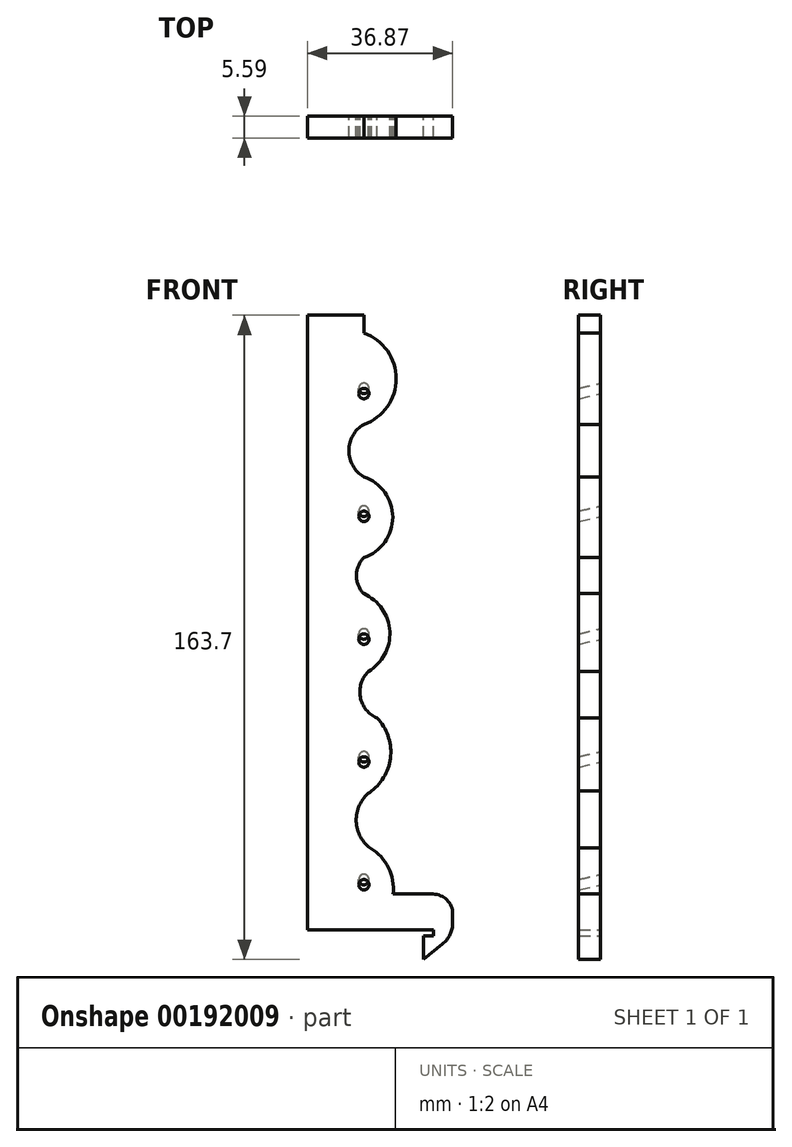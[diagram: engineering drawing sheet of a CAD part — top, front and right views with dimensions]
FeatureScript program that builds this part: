
annotation { "Feature Type Name" : "Feature", "Feature Type Description" : "" }
export const myFeature = defineFeature(function(context is Context, id is Id, definition is map)
    precondition{}
    {
        {
            var Q0;
            Q0=qCreatedBy(makeId("Front.planeOp"),FACE);
            var sketch = newSketch(context, id + "F0", { "sketchPlane" : qUnion([Q0])});
            skLineSegment(sketch, "E0", {"start": v(-18.92, 124.62) * mm, "end": v(-18.92, -31.58) * mm});
            skLineSegment(sketch, "E1", {"start": v(-18.92, 124.62) * mm, "end": v(-4.62, 124.62) * mm});
            skLineSegment(sketch, "E2", {"start": v(10.58, -33.08) * mm, "end": v(13.08, -33.08) * mm});
            skLineSegment(sketch, "E3", {"start": v(-18.92, -31.58) * mm, "end": v(13.08, -31.58) * mm});
            skLineSegment(sketch, "E4", {"start": v(13.08, -33.08) * mm, "end": v(13.08, -31.58) * mm});
            skLineSegment(sketch, "E5", {"start": v(10.58, -33.08) * mm, "end": v(10.58, -39.08) * mm});
            skLineSegment(sketch, "E6", {"start": v(10.58, -39.08) * mm, "end": v(17.95, -33.08) * mm});
            skLineSegment(sketch, "E7", {"start": v(17.95, -33.08) * mm, "end": v(17.95, -22.48) * mm});
            skLineSegment(sketch, "E8", {"start": v(17.95, -22.48) * mm, "end": v(2.81, -22.48) * mm});
            skArc(sketch, "E9", {"start": v(-3.49, 34.05) * mm, "mid": v(-5.5, 27.56) * mm, "end": v(-1.25, 22.25) * mm});
            skArc(sketch, "E10", {"start": v(2.81, -22.48) * mm, "mid": v(1.63, -15.76) * mm, "end": v(-3.02, -10.76) * mm});
            skArc(sketch, "E11", {"start": v(-2.68, 3.72) * mm, "mid": v(2.19, 12.67) * mm, "end": v(-1.25, 22.25) * mm});
            skArc(sketch, "E12", {"start": v(-2.68, 3.72) * mm, "mid": v(-6.55, -3.43) * mm, "end": v(-3.02, -10.76) * mm});
            skLineSegment(sketch, "E13", {"start": v(-4.62, -47.9) * mm, "end": v(-4.62, 124.62) * mm, "construction": true});
            skArc(sketch, "E14", {"start": v(-3.49, 34.05) * mm, "mid": v(1.96, 44.3) * mm, "end": v(-4.62, 53.85) * mm});
            skLineSegment(sketch, "E15", {"start": v(-4.62, 120.08) * mm, "end": v(-4.62, 124.62) * mm});
            skArc(sketch, "E16", {"start": v(-4.62, 63.01) * mm, "mid": v(-6.53, 58.43) * mm, "end": v(-4.62, 53.85) * mm});
            skArc(sketch, "E17", {"start": v(-4.62, 63.01) * mm, "mid": v(2.72, 73.28) * mm, "end": v(-4.62, 83.55) * mm});
            skArc(sketch, "E18", {"start": v(-4.62, 96.87) * mm, "mid": v(-8.44, 90.21) * mm, "end": v(-4.62, 83.55) * mm});
            skArc(sketch, "E19", {"start": v(-4.62, 96.87) * mm, "mid": v(3.6, 108.48) * mm, "end": v(-4.62, 120.08) * mm});
            skSolve(sketch);
        }
        {
            var Q0;
            Q0=qCreatedBy(makeId("Front.planeOp"),FACE);
            var sketch = newSketch(context, id + "F1", { "sketchPlane" : qUnion([Q0])});
            skLineSegment(sketch, "E20", {"start": v(-34.42, -18.78) * mm, "end": v(36.84, -18.78) * mm, "construction": true});
            skSolve(sketch);
        }
        {
            var Q0;
            Q0=qCreatedBy(makeId("Front.planeOp"),FACE);
            var sketch = newSketch(context, id + "F2", { "sketchPlane" : qUnion([Q0])});
            skLineSegment(sketch, "E21", {"start": v(24.36, 12.42) * mm, "end": v(-43.96, 12.42) * mm, "construction": true});
            skSolve(sketch);
        }
        {
            var Q0;
            Q0=qCreatedBy(makeId("Front.planeOp"),FACE);
            var sketch = newSketch(context, id + "F3", { "sketchPlane" : qUnion([Q0])});
            skLineSegment(sketch, "E22", {"start": v(22.2, 43.62) * mm, "end": v(-38.2, 43.62) * mm, "construction": true});
            skLineSegment(sketch, "E23", {"start": v(-44.47, 74.82) * mm, "end": v(24.47, 74.82) * mm, "construction": true});
            skLineSegment(sketch, "E24", {"start": v(-44.4, 106.02) * mm, "end": v(24.55, 106.02) * mm, "construction": true});
            skSolve(sketch);
        }
        {
            var Q0;
            Q0=sQuery(id+"F1.wireOp",EDGE,"E20");
            cPlane(context, id + "F4", {"entities" : qUnion([Q0]), "cplaneType" : CPlaneType.LINE_ANGLE, "offset" : 25 * mm, "angle" : 13.27 * degree, "width" : 150 * mm, "height" : 150 * mm});
        }
        {
            var Q0;
            Q0=sQuery(id+"F2.wireOp",EDGE,"E21");
            cPlane(context, id + "F5", {"entities" : qUnion([Q0]), "cplaneType" : CPlaneType.LINE_ANGLE, "offset" : 25 * mm, "angle" : 346.73 * degree, "width" : 150 * mm, "height" : 150 * mm});
        }
        {
            var Q0;
            Q0=sQuery(id+"F3.wireOp",EDGE,"E22");
            cPlane(context, id + "F6", {"entities" : qUnion([Q0]), "cplaneType" : CPlaneType.LINE_ANGLE, "offset" : 25 * mm, "angle" : 346.73 * degree, "width" : 150 * mm, "height" : 150 * mm});
        }
        {
            var Q0;
            Q0=qCreatedBy(id+"F4.planeOp",FACE);
            var sketch = newSketch(context, id + "F7", { "sketchPlane" : qUnion([Q0])});
            skCircle(sketch, "E25", {"center": v(4.62, -18.28) * mm, "radius": 1.3 * mm});
            skSolve(sketch);
        }
        {
            var Q0;
            Q0=qCreatedBy(id+"F5.planeOp",FACE);
            var sketch = newSketch(context, id + "F8", { "sketchPlane" : qUnion([Q0])});
            skCircle(sketch, "E26", {"center": v(-4.62, 12.09) * mm, "radius": 1.3 * mm});
            skSolve(sketch);
        }
        {
            var Q0;
            Q0=qCreatedBy(id+"F6.planeOp",FACE);
            var sketch = newSketch(context, id + "F9", { "sketchPlane" : qUnion([Q0])});
            skCircle(sketch, "E27", {"center": v(-4.62, 42.46) * mm, "radius": 1.3 * mm});
            skSolve(sketch);
        }
        {
            var Q0;
            Q0=sQuery(id+"F3.wireOp",EDGE,"E23");
            cPlane(context, id + "F10", {"entities" : qUnion([Q0]), "cplaneType" : CPlaneType.LINE_ANGLE, "offset" : 25 * mm, "angle" : 13.27 * degree, "width" : 150 * mm, "height" : 150 * mm});
        }
        {
            var Q0;
            Q0=sQuery(id+"F3.wireOp",EDGE,"E24");
            cPlane(context, id + "F11", {"entities" : qUnion([Q0]), "cplaneType" : CPlaneType.LINE_ANGLE, "offset" : 25 * mm, "angle" : 13.27 * degree, "width" : 150 * mm, "height" : 150 * mm});
        }
        {
            var Q0;
            Q0=qCreatedBy(id+"F10.planeOp",FACE);
            var sketch = newSketch(context, id + "F12", { "sketchPlane" : qUnion([Q0])});
            skCircle(sketch, "E28", {"center": v(4.62, 72.82) * mm, "radius": 1.3 * mm});
            skSolve(sketch);
        }
        {
            var Q0;
            Q0=qCreatedBy(id+"F11.planeOp",FACE);
            var sketch = newSketch(context, id + "F13", { "sketchPlane" : qUnion([Q0])});
            skCircle(sketch, "E29", {"center": v(4.62, 103.19) * mm, "radius": 1.3 * mm});
            skSolve(sketch);
        }
        {
            var Q0;
            Q0=makeQuery(id+"F0.imprint","IMPRINT",FACE,{"disambiguationData":[TD([[makeQuery(id+"F0.imprint","IMPRINT",EDGE,{"derivedFrom":sQuery(id+"F0.wireOp",EDGE,"E0")}),1.0]])]});
            extrude(context, id + "F14", {"entities" : qUnion([Q0]), "depth" : 5.6 * mm});
        }
        {
            var Q0;
            Q0 = qSketchRegion(id + "F7", true);
            var Q1;
            Q1 = qSketchRegion(id + "F8", true);
            var Q2;
            Q2 = qSketchRegion(id + "F9", true);
            var Q3;
            Q3 = qSketchRegion(id + "F13", true);
            var Q4;
            Q4 = qSketchRegion(id + "F12", true);
            extrude(context, id + "F15", {"entities" : qUnion([Q0, Q1, Q2, Q3, Q4]), "operationType" : NewBodyOperationType.REMOVE, "endBound" : BoundingType.SYMMETRIC, "oppositeDirection" : true, "depth" : 25 * mm});
        }
        {
            var Q0;
            Q0=makeQuery(id+"F14.opExtrude","SWEPT_EDGE",EDGE,{"disambiguationData":[OSD([sQuery(id+"F0.wireOp",EDGE,"E7"),sQuery(id+"F0.wireOp",EDGE,"E8")])]});
            fillet(context, id + "F16", {"entities" : qUnion([Q0]), "radius" : 5 * mm, "tangentPropagation" : true, "allowEdgeOverflow" : false});
        }
        {
            var Q0;
            Q0=makeQuery(id+"F14.opExtrude","SWEPT_EDGE",EDGE,{"disambiguationData":[OSD([sQuery(id+"F0.wireOp",EDGE,"E6"),sQuery(id+"F0.wireOp",EDGE,"E7")])]});
            fillet(context, id + "F17", {"entities" : qUnion([Q0]), "radius" : 7 * mm, "tangentPropagation" : true, "allowEdgeOverflow" : false});
        }
    });
